# Revit family: BV1250
name_source: partatom
category: Plumbing Fixtures
revit_build: Autodesk Revit Structure 2013 (Build: 20120221_2030(x64)
units: mm (PartAtom-declared; Revit-internal decimal feet)

## types (3) — shared parameters
Body Material = Brass
Description = Brass backwater valve with neoprene seat
Manufacturer = Mifab
Model = BV1250
URL = www.mifab.com
material = Neoprine seat

## per-type parameters (varying)
| type | HOLES 1 | HOLES 2 | HOLES 3 | Height | Height 2 | Height 3 | Height 4 | Heright 1 | Inner | Pipe size | Screw Hole | Thickness 2 | Thickness of Pepe size | Upper |
| BV1250-2' | 0' - 5 11/32" | 0' - 6 5/16" | 0' - 0 19/32" | 0' - 9 19/32" | 0' - 3 27/32" | 0' - 2 11/16" | 1' - 1 7/16" | 0' - 5 3/4" | 0' - 2 13/32" | 1' - 0" | 0' - 0 15/32" | 0' - 5 13/32" | 0' - 6" | 0' - 1 19/32" |
| BV1250-3' | 0' - 8" | 0' - 9 15/32" | 0' - 0 29/32" | 1' - 2 13/32" | 0' - 5 3/4" | 0' - 4 1/32" | 1' - 8 5/32" | 0' - 8 5/8" | 0' - 3 19/32" | 1' - 6" | 0' - 0 23/32" | 0' - 8 3/32" | 0' - 9" | 0' - 2 13/32" |
| BV1250-4' | 0' - 10 21/32" | 1' - 0 5/8" | 0' - 1 3/16" | 1' - 7 5/32" | 0' - 7 21/32" | 0' - 5 3/8" | 2' - 2 27/32" | 0' - 11 1/2" | 0' - 4 25/32" | 1' - 11 31/32" | 0' - 0 31/32" | 0' - 10 25/32" | 0' - 11 31/32" | 0' - 3 3/16" |

## geometry (parser evidence)
native form markers: Sweep x1
no freeform markers — native parametric forms only
